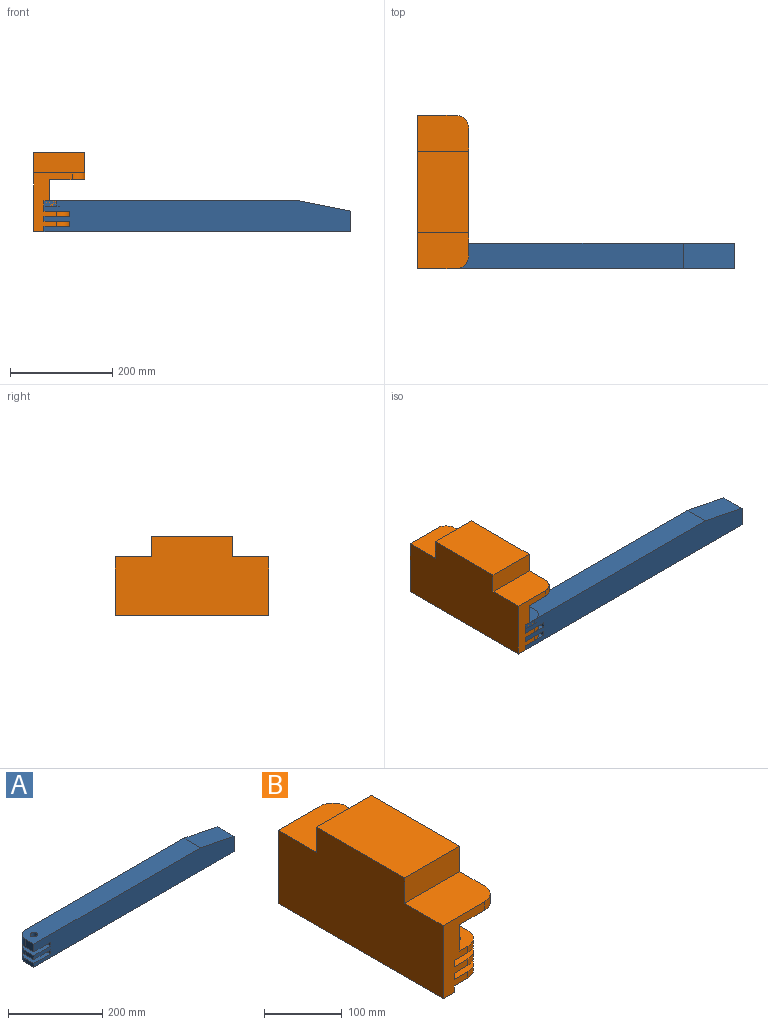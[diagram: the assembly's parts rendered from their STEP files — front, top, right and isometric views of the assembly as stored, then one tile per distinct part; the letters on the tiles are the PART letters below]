
ASSEMBLY  parts=2 mates=1
PART A: 21 faces, bbox 600x50x60 mm
  f0: plane 50x40mm, normal (1,0,0), area 2000mm2, adj f11,f12,f13,f20
  f1: plane 500x50mm, normal (0,0,1), area 24664.8mm2, adj f2,f12,f13,f16,f19,f20
  f2: plane 25x20mm, normal (-1,0,0), area 500mm2, adj f1,f3,f12,f16
  f3: plane 50x50mm, normal (0,0,-1), area 2164.8mm2, adj f2,f4,f12,f13,f16,f19
  f4: plane 50x10mm, normal (-1,0,0), area 500mm2, adj f3,f5,f12,f13
  f5: plane 50x50mm, normal (0,0,1), area 2164.8mm2, adj f4,f6,f12,f13,f15,f18
  f6: plane 25x10mm, normal (-1,0,0), area 250mm2, adj f5,f7,f12,f15
  f7: plane 50x50mm, normal (0,0,-1), area 2164.8mm2, adj f6,f8,f12,f13,f15,f18
  f8: plane 50x10mm, normal (-1,0,0), area 500mm2, adj f7,f9,f12,f13
  f9: plane 50x50mm, normal (0,0,1), area 2164.8mm2, adj f8,f10,f12,f13,f14,f17
  f10: plane 25x10mm, normal (-1,0,0), area 250mm2, adj f9,f11,f12,f14
  f11: plane 600x50mm, normal (0,0,-1), area 29865.9mm2, adj f0,f10,f12,f13,f14
  f12: plane 600x60mm, normal (0,-1,0), area 34000mm2, adj f0,f1,f2,f3,f4,f5,f6,f7
  f13: plane 575x60mm, normal (0,1,0), area 33000mm2, adj f0,f1,f3,f4,f5,f7,f8,f9
  f14: cylinder r=25mm len=25mm, axis (0,0,-1), area 392.7mm2, adj f9,f10,f11,f13
  f15: cylinder r=25mm len=25mm, axis (0,0,-1), area 392.7mm2, adj f5,f6,f7,f13
  f16: cylinder r=25mm len=25mm, axis (0,0,-1), area 785.4mm2, adj f1,f2,f3,f13
  f17: cone r=0mm half-angle=59deg, axis (0,0,1), area 234.6mm2, adj f9
  f18: cylinder r=8mm len=16mm, axis (0,0,1), area 502.7mm2, adj f5,f7
  f19: cylinder r=8mm len=20mm, axis (0,0,1), area 1005.3mm2, adj f1,f3
  f20: plane 100x50mm, normal (0.2,0,0.98), area 5099mm2, adj f0,f1,f12,f13
PART B: 33 faces, bbox 100x300x155 mm
  f0: plane 115x75mm, normal (0,-1,0), area 4208.6mm2, adj f5,f6,f7,f8,f9,f13,f14,f15
  f1: plane 275x60mm, normal (1,0,0), area 15750mm2, adj f4,f6,f7,f14,f15,f16,f18,f19
  f2: plane 160x100mm, normal (0,0,1), area 16000mm2, adj f3,f5,f11,f12
  f3: plane 250x53.53mm, normal (1,0,0), area 9781.3mm2, adj f2,f9,f10,f11,f12,f13,f30,f32
  f4: plane 115x75mm, normal (0,1,0), area 6458.6mm2, adj f1,f5,f6,f7,f8,f9,f10,f30
  f5: plane 300x155mm, normal (-1,0,0), area 40900mm2, adj f0,f2,f4,f6,f10,f11,f12,f13
  f6: plane 300x70mm, normal (0,0,-1), area 18500mm2, adj f0,f1,f4,f5,f23,f24
  f7: plane 300x40mm, normal (0,0,1), area 11664.8mm2, adj f0,f1,f4,f8,f27,f31
  f8: plane 300x41.48mm, normal (1,0,0), area 12442.5mm2, adj f0,f4,f7,f9
  f9: plane 300x70mm, normal (0,0,-1), area 20731.7mm2, adj f0,f3,f4,f8,f30,f32
  f10: plane 100x70mm, normal (0,0,1), area 6865.9mm2, adj f3,f4,f5,f11,f30
  f11: plane 100x40mm, normal (0,1,0), area 4000mm2, adj f2,f3,f5,f10
  f12: plane 100x40mm, normal (0,-1,0), area 4000mm2, adj f2,f3,f5,f13
  f13: plane 100x70mm, normal (0,0,1), area 6865.9mm2, adj f0,f3,f5,f12,f32
  f14: plane 50x50mm, normal (0,0,-1), area 2164.8mm2, adj f0,f1,f16,f17,f26,f29
  f15: plane 50x50mm, normal (0,0,1), area 2164.8mm2, adj f0,f1,f16,f17,f25,f28
  f16: plane 50x10mm, normal (0,-1,0), area 500mm2, adj f1,f14,f15,f17
  f17: plane 50x10mm, normal (1,0,0), area 500mm2, adj f0,f14,f15,f16
  f18: plane 50x50mm, normal (0,0,-1), area 2164.8mm2, adj f0,f1,f20,f21,f27,f31
  f19: plane 50x50mm, normal (0,0,1), area 2164.8mm2, adj f0,f1,f20,f21,f26,f29
  f20: plane 50x10mm, normal (0,-1,0), area 500mm2, adj f1,f18,f19,f21
  f21: plane 50x10mm, normal (1,0,0), area 500mm2, adj f0,f18,f19,f20
  f22: plane 50x50mm, normal (0,0,-1), area 2164.8mm2, adj f0,f1,f23,f24,f25,f28
  f23: plane 50x10mm, normal (0,-1,0), area 500mm2, adj f1,f6,f22,f24
  f24: plane 50x10mm, normal (1,0,0), area 500mm2, adj f0,f6,f22,f23
  f25: cylinder r=8mm len=16mm, axis (0,0,-1), area 502.7mm2, adj f15,f22
  f26: cylinder r=8mm len=16mm, axis (0,0,-1), area 502.7mm2, adj f14,f19
  f27: cylinder r=8mm len=16mm, axis (0,0,-1), area 502.7mm2, adj f7,f18
  f28: cylinder r=25mm len=25mm, axis (0,0,-1), area 392.7mm2, adj f0,f1,f15,f22
  f29: cylinder r=25mm len=25mm, axis (0,0,-1), area 392.7mm2, adj f0,f1,f14,f19
  f30: cylinder r=25mm len=25mm, axis (0,0,1), area 531.1mm2, adj f3,f4,f9,f10
  f31: cylinder r=25mm len=25mm, axis (0,0,-1), area 392.7mm2, adj f0,f1,f7,f18
  f32: cylinder r=25mm len=25mm, axis (0,0,-1), area 531.1mm2, adj f0,f3,f9,f13
PLACE A t=(40.78,-142.82,-71.69)mm
PLACE B t=(-35.85,107.18,-26.65)mm
MATE revolute A.f14 <-> B.f25  axis (0,0,1) through (-56.79,-167.82,-36.88)mm
